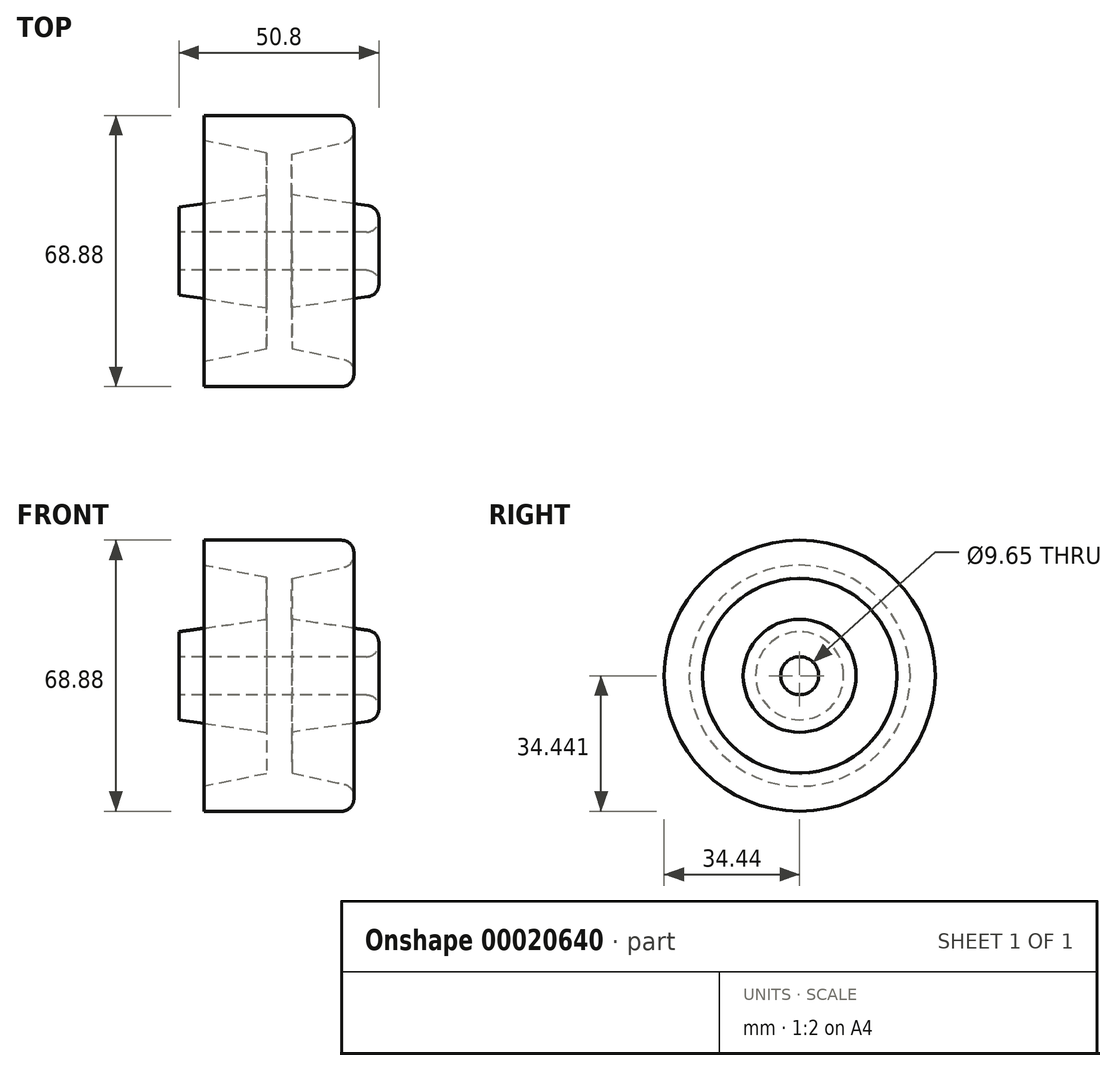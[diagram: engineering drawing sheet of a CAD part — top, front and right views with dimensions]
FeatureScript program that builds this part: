
annotation { "Feature Type Name" : "Feature", "Feature Type Description" : "" }
export const myFeature = defineFeature(function(context is Context, id is Id, definition is map)
    precondition{}
    {
        {
            var Q0;
            Q0=qCreatedBy(makeId("Front.planeOp"),FACE);
            var sketch = newSketch(context, id + "F0", { "sketchPlane" : qUnion([Q0])});
            skLineSegment(sketch, "E0", {"start": v(-28.73, 12.93) * mm, "end": v(22.07, 12.93) * mm});
            skLineSegment(sketch, "E1", {"start": v(22.07, 12.93) * mm, "end": v(22.07, 6.58) * mm});
            skLineSegment(sketch, "E2", {"start": v(15.72, -10.34) * mm, "end": v(15.72, -16.69) * mm});
            skLineSegment(sketch, "E3", {"start": v(15.72, -16.69) * mm, "end": v(-22.38, -16.69) * mm});
            skLineSegment(sketch, "E4", {"start": v(-22.38, -16.69) * mm, "end": v(-22.38, -10.34) * mm});
            skLineSegment(sketch, "E5", {"start": v(-6.5, -7.16) * mm, "end": v(-6.5, 3.4) * mm});
            skLineSegment(sketch, "E6", {"start": v(-28.73, 12.93) * mm, "end": v(-28.73, 6.58) * mm});
            skLineSegment(sketch, "E7", {"start": v(-22.38, -10.34) * mm, "end": v(-6.5, -7.16) * mm});
            skLineSegment(sketch, "E8", {"start": v(15.72, -10.34) * mm, "end": v(0, -6.94) * mm});
            skLineSegment(sketch, "E9", {"start": v(-6.5, 3.4) * mm, "end": v(-28.73, 6.58) * mm});
            skLineSegment(sketch, "E10", {"start": v(-0.15, 3.4) * mm, "end": v(22.07, 6.58) * mm});
            skPoint(sketch, "E11.end.orphan", {"position": v(-28.84, 3.4) * mm});
            skPoint(sketch, "E12.start.orphan", {"position": v(15.72, -6.94) * mm});
            skPoint(sketch, "E13.start.orphan", {"position": v(-0.15, 6.58) * mm});
            skPoint(sketch, "E14.end.orphan", {"position": v(-6.5, 6.58) * mm});
            skLineSegment(sketch, "E15", {"start": v(-0.15, 3.4) * mm, "end": v(0, -6.94) * mm});
            skLineSegment(sketch, "E16", {"start": v(-28.65, 17.75) * mm, "end": v(22.15, 17.75) * mm});
            skSolve(sketch);
        }
        {
            var Q0;
            Q0=makeQuery(id+"F0.imprint","IMPRINT",FACE,{"disambiguationData":[TD([[makeQuery(id+"F0.imprint","IMPRINT",EDGE,{"derivedFrom":sQuery(id+"F0.wireOp",EDGE,"E0")}),-1.0]])]});
            var Q1;
            Q1=sQuery(id+"F0.wireOp",EDGE,"E16");
            revolve(context, id + "F1", {"entities" : qUnion([Q0]), "axis" : qUnion([Q1]), "revolveType" : RevolveType.FULL});
        }
        {
            var Q0;
            Q0=makeQuery(id+"F1.opRevolve","SWEPT_EDGE",EDGE,{"disambiguationData":[OSD([sQuery(id+"F0.wireOp",EDGE,"E2"),sQuery(id+"F0.wireOp",EDGE,"E3")])]});
            var Q1;
            Q1=makeQuery(id+"F1.opRevolve","SWEPT_EDGE",EDGE,{"disambiguationData":[OSD([sQuery(id+"F0.wireOp",EDGE,"E2"),sQuery(id+"F0.wireOp",EDGE,"E8")])]});
            var Q2;
            Q2=makeQuery(id+"F1.opRevolve","SWEPT_EDGE",EDGE,{"disambiguationData":[OSD([sQuery(id+"F0.wireOp",EDGE,"E1"),sQuery(id+"F0.wireOp",EDGE,"E10")])]});
            var Q3;
            Q3=makeQuery(id+"F1.opRevolve","SWEPT_EDGE",EDGE,{"disambiguationData":[OSD([sQuery(id+"F0.wireOp",EDGE,"E0"),sQuery(id+"F0.wireOp",EDGE,"E1")])]});
            fillet(context, id + "F2", {"entities" : qUnion([Q0, Q1, Q2, Q3]), "radius" : 3.17 * mm, "tangentPropagation" : true, "allowEdgeOverflow" : false});
        }
    });
